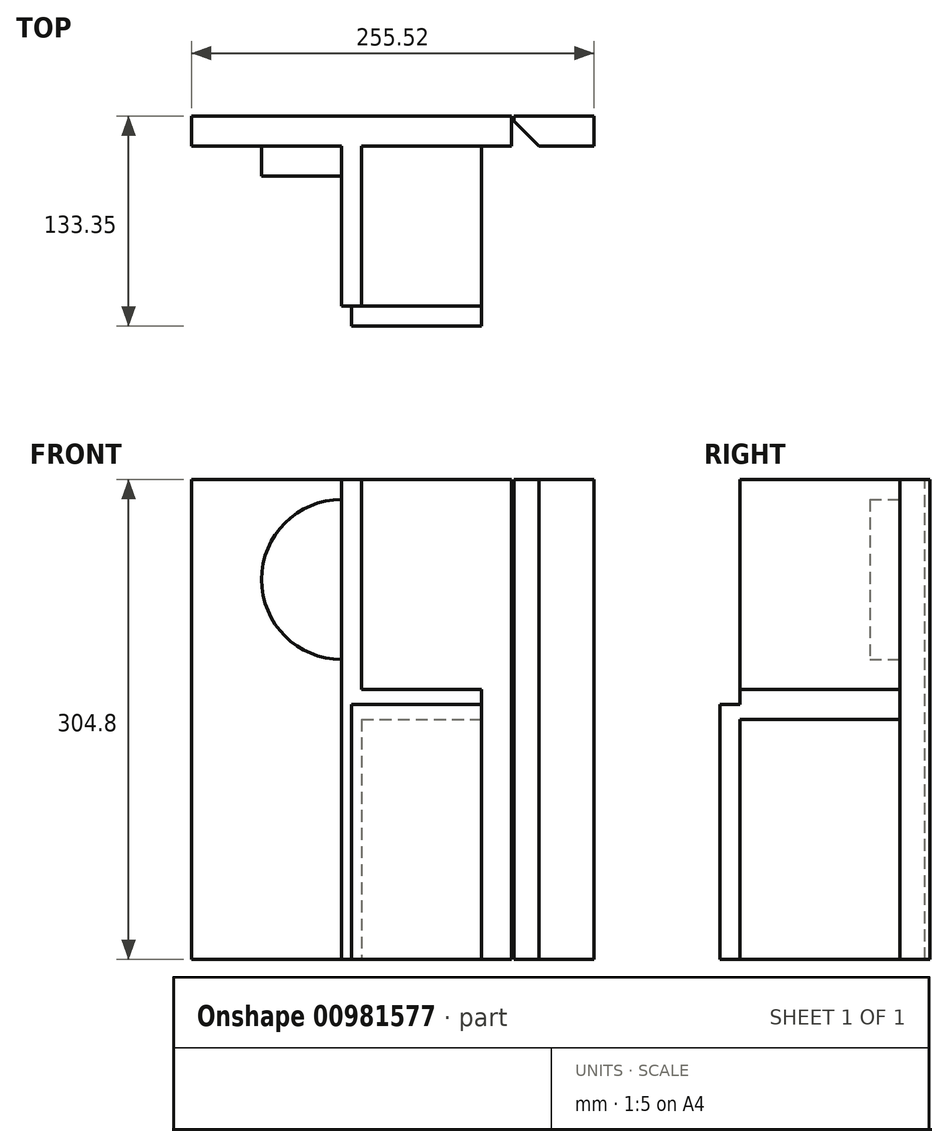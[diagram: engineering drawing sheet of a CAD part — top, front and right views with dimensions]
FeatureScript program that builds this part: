
annotation { "Feature Type Name" : "Feature", "Feature Type Description" : "" }
export const myFeature = defineFeature(function(context is Context, id is Id, definition is map)
    precondition{}
    {
        {
            var Q0;
            Q0=qCreatedBy(makeId("Front.planeOp"),FACE);
            var sketch = newSketch(context, id + "F0", { "sketchPlane" : qUnion([Q0])});
            skLineSegment(sketch, "E0.bottom", {"start": v(101.6, -152.4) * mm, "end": v(-101.6, -152.4) * mm});
            skLineSegment(sketch, "E0.top", {"start": v(101.6, 152.4) * mm, "end": v(-101.6, 152.4) * mm});
            skLineSegment(sketch, "E0.left", {"start": v(101.6, -152.4) * mm, "end": v(101.6, 152.4) * mm});
            skLineSegment(sketch, "E0.right", {"start": v(-101.6, -152.4) * mm, "end": v(-101.6, 152.4) * mm});
            skPoint(sketch, "E0.middle", {"position": v(0, 0) * mm});
            skLineSegment(sketch, "E1.left", {"start": v(101.6, -152.4) * mm, "end": v(101.6, -153.13) * mm});
            skLineSegment(sketch, "E2.bottom", {"start": v(103.12, 152.4) * mm, "end": v(153.92, 152.4) * mm});
            skLineSegment(sketch, "E2.top", {"start": v(103.12, -152.4) * mm, "end": v(153.92, -152.4) * mm});
            skLineSegment(sketch, "E2.left", {"start": v(103.12, 152.4) * mm, "end": v(103.12, -152.4) * mm});
            skLineSegment(sketch, "E2.right", {"start": v(153.92, 152.4) * mm, "end": v(153.92, -152.4) * mm});
            skLineSegment(sketch, "E3.top", {"start": v(-6.35, -152.4) * mm, "end": v(6.35, -152.4) * mm});
            skSolve(sketch);
        }
        {
            var Q0;
            Q0=makeQuery(id+"F0.imprint","IMPRINT",FACE,{"disambiguationData":[TD([[makeQuery(id+"F0.imprint","IMPRINT",EDGE,{"derivedFrom":sQuery(id+"F0.wireOp",EDGE,"E2.bottom")}),-1.0]])]});
            var Q1;
            Q1=makeQuery(id+"F0.imprint","IMPRINT",FACE,{"disambiguationData":[TD([[makeQuery(id+"F0.imprint","IMPRINT",EDGE,{"derivedFrom":sQuery(id+"F0.wireOp",EDGE,"E0.top")}),1.0]])]});
            extrude(context, id + "F1", {"entities" : qUnion([Q0, Q1]), "oppositeDirection" : true, "depth" : 19.05 * mm, "offsetDistance" : 25.4 * mm});
        }
        {
            var Q0;
            Q0=makeQuery(id+"F1.opExtrude","CAP_EDGE",EDGE,{"disambiguationData":[OSD([sQuery(id+"F0.wireOp",EDGE,"E2.left")])],"isStart":true});
            chamfer(context, id + "F2", {"entities" : qUnion([Q0]), "width" : 15.88 * mm, "tangentPropagation" : true});
        }
        {
            var Q0;
            Q0=makeQuery(id+"F1.opExtrude","CAP_FACE",FACE,{"disambiguationData":[OSD([sQuery(id+"F0.wireOp",EDGE,"E0.bottom"),sQuery(id+"F0.wireOp",EDGE,"E0.top"),sQuery(id+"F0.wireOp",EDGE,"E0.left"),sQuery(id+"F0.wireOp",EDGE,"E0.right"),sQuery(id+"F0.wireOp",EDGE,"E3.top")])],"isStart":true});
            var sketch = newSketch(context, id + "F3", { "sketchPlane" : qUnion([Q0])});
            skLineSegment(sketch, "E4.bottom", {"start": v(-6.35, 152.4) * mm, "end": v(6.35, 152.4) * mm});
            skLineSegment(sketch, "E4.top", {"start": v(-6.35, -152.4) * mm, "end": v(6.35, -152.4) * mm});
            skLineSegment(sketch, "E4.left", {"start": v(-6.35, 152.4) * mm, "end": v(-6.35, -152.4) * mm});
            skLineSegment(sketch, "E4.right", {"start": v(6.35, 152.4) * mm, "end": v(6.35, -152.4) * mm});
            skPoint(sketch, "E4.middle", {"position": v(0, 0) * mm});
            skLineSegment(sketch, "E5.bottom", {"start": v(6.35, 0) * mm, "end": v(82.55, 0) * mm});
            skLineSegment(sketch, "E5.top", {"start": v(6.35, 19.05) * mm, "end": v(82.55, 19.05) * mm});
            skLineSegment(sketch, "E5.left", {"start": v(6.35, 0) * mm, "end": v(6.35, 19.05) * mm});
            skLineSegment(sketch, "E5.right", {"start": v(82.55, 0) * mm, "end": v(82.55, 19.05) * mm});
            skSolve(sketch);
        }
        {
            var Q0;
            {var subQ1=sQuery(id+"F3.wireOp",EDGE,"E4.bottom");Q0=makeQuery(id+"F3.imprint","IMPRINT",FACE,{"disambiguationData":[TD([[makeQuery(id+"F3.imprint","IMPRINT",EDGE,{"derivedFrom":subQ1}),1.0]])]});}
            var Q1;
            Q1=makeQuery(id+"F3.imprint","IMPRINT",FACE,{"disambiguationData":[TD([[makeQuery(id+"F3.imprint","IMPRINT",EDGE,{"derivedFrom":sQuery(id+"F3.wireOp",EDGE,"E5.bottom")}),1.0]])]});
            extrude(context, id + "F4", {"entities" : qUnion([Q0, Q1]), "operationType" : NewBodyOperationType.ADD, "depth" : 101.6 * mm, "offsetDistance" : 25.4 * mm});
        }
        {
            var Q0;
            {var subQ0=sQuery(id+"F0.wireOp",EDGE,"E0.right");var subQ1=sQuery(id+"F0.wireOp",EDGE,"E0.top");var subQ2=sQuery(id+"F0.wireOp",EDGE,"E3.top");var subQ3=sQuery(id+"F0.wireOp",EDGE,"E0.bottom");Q0=makeQuery(id+"F4.boolean.opBoolean","SPLIT",FACE,{"disambiguationData":[TD([makeQuery(id+"F1.opExtrude","SWEPT_FACE",FACE,{"disambiguationData":[OSD([subQ0])]})])],"derivedFrom":makeQuery(id+"F1.opExtrude","CAP_FACE",FACE,{"disambiguationData":[OSD([subQ3,subQ1,sQuery(id+"F0.wireOp",EDGE,"E0.left"),subQ0,subQ2])],"isStart":true})});}
            var sketch = newSketch(context, id + "F5", { "sketchPlane" : qUnion([Q0])});
            skArc(sketch, "E6", {"start": v(-6.35, 139.7) * mm, "mid": v(-57.15, 88.9) * mm, "end": v(-6.35, 38.1) * mm});
            skSolve(sketch);
        }
        {
            var Q0;
            {var subQ0=sQuery(id+"F5.wireOp",EDGE,"E6");Q0=makeQuery(id+"F5.imprint","IMPRINT",FACE,{"disambiguationData":[TD([[makeQuery(id+"F5.imprint","IMPRINT",EDGE,{"derivedFrom":subQ0}),1.0]])]});}
            extrude(context, id + "F6", {"entities" : qUnion([Q0]), "operationType" : NewBodyOperationType.ADD, "depth" : 19.05 * mm, "offsetDistance" : 25.4 * mm});
        }
        {
            var Q0;
            Q0=makeQuery(id+"F4.opExtrude","CAP_FACE",FACE,{"disambiguationData":[OSD([sQuery(id+"F3.wireOp",EDGE,"E4.bottom"),sQuery(id+"F3.wireOp",EDGE,"E4.top"),sQuery(id+"F3.wireOp",EDGE,"E4.left"),sQuery(id+"F3.wireOp",EDGE,"E4.right"),sQuery(id+"F3.wireOp",EDGE,"E5.bottom"),sQuery(id+"F3.wireOp",EDGE,"E5.top"),sQuery(id+"F3.wireOp",EDGE,"E5.right")])],"isStart":false});
            var sketch = newSketch(context, id + "F7", { "sketchPlane" : qUnion([Q0])});
            skLineSegment(sketch, "E7.bottom", {"start": v(0, -152.4) * mm, "end": v(82.55, -152.4) * mm});
            skLineSegment(sketch, "E7.top", {"start": v(0, 9.52) * mm, "end": v(82.55, 9.52) * mm});
            skLineSegment(sketch, "E7.left", {"start": v(0, -152.4) * mm, "end": v(0, 9.52) * mm});
            skLineSegment(sketch, "E7.right", {"start": v(82.55, -152.4) * mm, "end": v(82.55, 9.52) * mm});
            skSolve(sketch);
        }
        {
            var Q0;
            Q0 = qSketchRegion(id + "F7", true);
            extrude(context, id + "F8", {"entities" : qUnion([Q0]), "operationType" : NewBodyOperationType.ADD, "depth" : 12.7 * mm, "offsetDistance" : 25.4 * mm});
        }
    });
